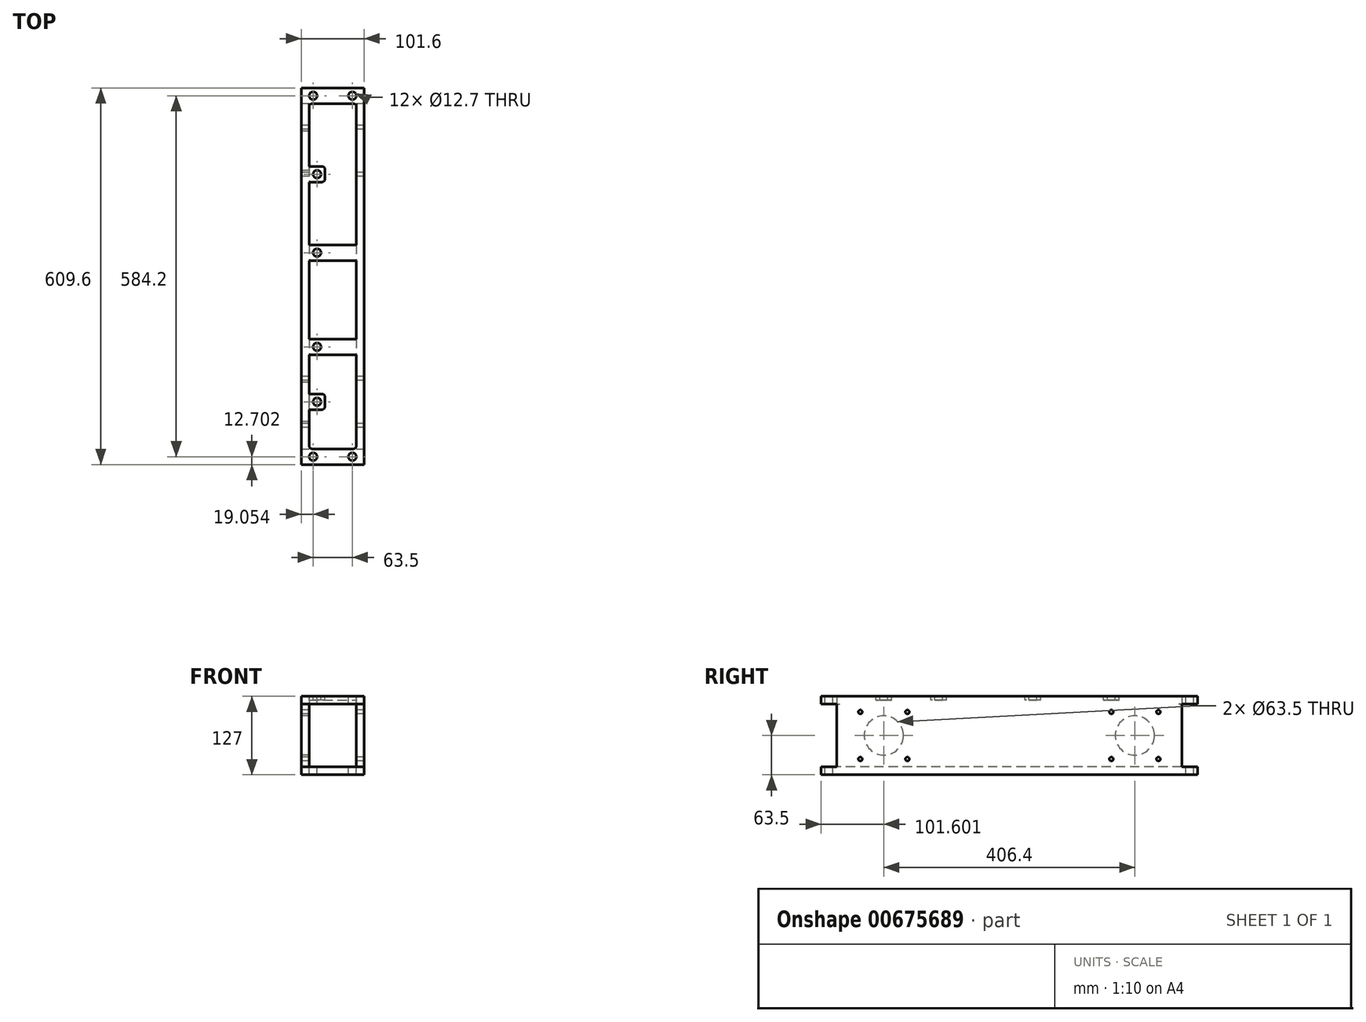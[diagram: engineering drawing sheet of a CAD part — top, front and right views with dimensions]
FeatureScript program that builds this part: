
annotation { "Feature Type Name" : "Feature", "Feature Type Description" : "" }
export const myFeature = defineFeature(function(context is Context, id is Id, definition is map)
    precondition{}
    {
        {
            var Q0;
            Q0=qCreatedBy(makeId("Top.planeOp"),FACE);
            var sketch = newSketch(context, id + "F0", { "sketchPlane" : qUnion([Q0])});
            skLineSegment(sketch, "E0.bottom", {"start": v(-138.95, -277.45) * mm, "end": v(-37.35, -277.45) * mm});
            skLineSegment(sketch, "E0.top", {"start": v(-138.95, 332.15) * mm, "end": v(-37.35, 332.15) * mm});
            skLineSegment(sketch, "E0.left", {"start": v(-138.95, -277.45) * mm, "end": v(-138.95, 332.15) * mm});
            skLineSegment(sketch, "E0.right", {"start": v(-37.35, -277.45) * mm, "end": v(-37.35, 332.15) * mm});
            skLineSegment(sketch, "E1.bottom", {"start": v(-126.25, 306.75) * mm, "end": v(-50.05, 306.75) * mm});
            skLineSegment(sketch, "E1.top", {"start": v(-126.25, -252.05) * mm, "end": v(-50.05, -252.05) * mm});
            skLineSegment(sketch, "E1.left", {"start": v(-126.25, 306.75) * mm, "end": v(-126.25, -252.05) * mm});
            skLineSegment(sketch, "E1.right", {"start": v(-50.05, 306.75) * mm, "end": v(-50.05, -252.05) * mm});
            skSolve(sketch);
        }
        {
            var Q0;
            Q0=makeQuery(id+"F0.imprint","IMPRINT",FACE,{"disambiguationData":[TD([[makeQuery(id+"F0.imprint","IMPRINT",EDGE,{"derivedFrom":sQuery(id+"F0.wireOp",EDGE,"E0.bottom")}),1.0]])]});
            extrude(context, id + "F1", {"entities" : qUnion([Q0]), "depth" : 127 * mm, "offsetDistance" : 25.4 * mm});
        }
        {
            var Q0;
            Q0=makeQuery(id+"F1.opExtrude","CAP_FACE",FACE,{"disambiguationData":[OSD([sQuery(id+"F0.wireOp",EDGE,"E0.bottom"),sQuery(id+"F0.wireOp",EDGE,"E0.top"),sQuery(id+"F0.wireOp",EDGE,"E0.left"),sQuery(id+"F0.wireOp",EDGE,"E0.right"),sQuery(id+"F0.wireOp",EDGE,"E1.bottom"),sQuery(id+"F0.wireOp",EDGE,"E1.top"),sQuery(id+"F0.wireOp",EDGE,"E1.left"),sQuery(id+"F0.wireOp",EDGE,"E1.right")])],"isStart":true});
            var sketch = newSketch(context, id + "F2", { "sketchPlane" : qUnion([Q0])});
            skLineSegment(sketch, "E2.bottom", {"start": v(-126.25, 252.05) * mm, "end": v(-50.05, 252.05) * mm});
            skLineSegment(sketch, "E2.top", {"start": v(-126.25, -306.75) * mm, "end": v(-50.05, -306.75) * mm});
            skLineSegment(sketch, "E2.left", {"start": v(-126.25, 252.05) * mm, "end": v(-126.25, -306.75) * mm});
            skLineSegment(sketch, "E2.right", {"start": v(-50.05, 252.05) * mm, "end": v(-50.05, -306.75) * mm});
            skSolve(sketch);
        }
        {
            var Q0;
            Q0=makeQuery(id+"F2.imprint","IMPRINT",FACE,{"disambiguationData":[TD([[makeQuery(id+"F2.imprint","IMPRINT",EDGE,{"derivedFrom":sQuery(id+"F2.wireOp",EDGE,"E2.bottom")}),-1.0]])]});
            extrude(context, id + "F3", {"entities" : qUnion([Q0]), "operationType" : NewBodyOperationType.ADD, "oppositeDirection" : true, "depth" : 19.05 * mm, "offsetDistance" : 25.4 * mm});
        }
        {
            var Q0;
            Q0=makeQuery(id+"F1.opExtrude","CAP_FACE",FACE,{"disambiguationData":[OSD([sQuery(id+"F0.wireOp",EDGE,"E0.bottom"),sQuery(id+"F0.wireOp",EDGE,"E0.top"),sQuery(id+"F0.wireOp",EDGE,"E0.left"),sQuery(id+"F0.wireOp",EDGE,"E0.right"),sQuery(id+"F0.wireOp",EDGE,"E1.bottom"),sQuery(id+"F0.wireOp",EDGE,"E1.top"),sQuery(id+"F0.wireOp",EDGE,"E1.left"),sQuery(id+"F0.wireOp",EDGE,"E1.right")])],"isStart":false});
            var sketch = newSketch(context, id + "F4", { "sketchPlane" : qUnion([Q0])});
            skLineSegment(sketch, "E3.bottom", {"start": v(-126.25, 78.15) * mm, "end": v(-50.05, 78.15) * mm});
            skLineSegment(sketch, "E3.top", {"start": v(-126.25, 52.75) * mm, "end": v(-50.05, 52.75) * mm});
            skLineSegment(sketch, "E3.left", {"start": v(-126.25, 78.15) * mm, "end": v(-126.25, 52.75) * mm});
            skLineSegment(sketch, "E3.right", {"start": v(-50.05, 78.15) * mm, "end": v(-50.05, 52.75) * mm});
            skLineSegment(sketch, "E4.bottom", {"start": v(-126.25, -74.25) * mm, "end": v(-50.05, -74.25) * mm});
            skLineSegment(sketch, "E4.top", {"start": v(-126.25, -99.65) * mm, "end": v(-50.05, -99.65) * mm});
            skLineSegment(sketch, "E4.left", {"start": v(-126.25, -74.25) * mm, "end": v(-126.25, -99.65) * mm});
            skLineSegment(sketch, "E4.right", {"start": v(-50.05, -74.25) * mm, "end": v(-50.05, -99.65) * mm});
            skSolve(sketch);
        }
        {
            var Q0;
            Q0=makeQuery(id+"F4.imprint","IMPRINT",FACE,{"disambiguationData":[TD([[makeQuery(id+"F4.imprint","IMPRINT",EDGE,{"derivedFrom":sQuery(id+"F4.wireOp",EDGE,"E3.bottom")}),-1.0]])]});
            var Q1;
            Q1=makeQuery(id+"F4.imprint","IMPRINT",FACE,{"disambiguationData":[TD([[makeQuery(id+"F4.imprint","IMPRINT",EDGE,{"derivedFrom":sQuery(id+"F4.wireOp",EDGE,"E4.bottom")}),-1.0]])]});
            extrude(context, id + "F5", {"entities" : qUnion([Q0, Q1]), "operationType" : NewBodyOperationType.ADD, "oppositeDirection" : true, "depth" : 6.35 * mm, "offsetDistance" : 25.4 * mm});
        }
        {
            var Q0;
            Q0=makeQuery(id+"F1.opExtrude","SWEPT_FACE",FACE,{"disambiguationData":[OSD([sQuery(id+"F0.wireOp",EDGE,"E0.bottom")])]});
            var sketch = newSketch(context, id + "F6", { "sketchPlane" : qUnion([Q0])});
            skLineSegment(sketch, "E5.bottom", {"start": v(-138.95, 114.3) * mm, "end": v(-37.35, 114.3) * mm});
            skLineSegment(sketch, "E5.top", {"start": v(-138.95, 12.7) * mm, "end": v(-37.35, 12.7) * mm});
            skLineSegment(sketch, "E5.left", {"start": v(-138.95, 114.3) * mm, "end": v(-138.95, 12.7) * mm});
            skLineSegment(sketch, "E5.right", {"start": v(-37.35, 114.3) * mm, "end": v(-37.35, 12.7) * mm});
            skSolve(sketch);
        }
        {
            var Q0;
            Q0=makeQuery(id+"F6.imprint","IMPRINT",FACE,{"disambiguationData":[TD([[makeQuery(id+"F6.imprint","IMPRINT",EDGE,{"derivedFrom":sQuery(id+"F6.wireOp",EDGE,"E5.bottom")}),-1.0]])]});
            extrude(context, id + "F7", {"entities" : qUnion([Q0]), "operationType" : NewBodyOperationType.REMOVE, "oppositeDirection" : true, "depth" : 25.4 * mm, "offsetDistance" : 25.4 * mm});
        }
        {
            var Q0;
            Q0=makeQuery(id+"F1.opExtrude","SWEPT_FACE",FACE,{"disambiguationData":[OSD([sQuery(id+"F0.wireOp",EDGE,"E0.top")])]});
            var sketch = newSketch(context, id + "F8", { "sketchPlane" : qUnion([Q0])});
            skLineSegment(sketch, "E6.bottom", {"start": v(37.35, 114.3) * mm, "end": v(138.95, 114.3) * mm});
            skLineSegment(sketch, "E6.top", {"start": v(37.35, 12.7) * mm, "end": v(138.95, 12.7) * mm});
            skLineSegment(sketch, "E6.left", {"start": v(37.35, 114.3) * mm, "end": v(37.35, 12.7) * mm});
            skLineSegment(sketch, "E6.right", {"start": v(138.95, 114.3) * mm, "end": v(138.95, 12.7) * mm});
            skSolve(sketch);
        }
        {
            var Q0;
            Q0=makeQuery(id+"F8.imprint","IMPRINT",FACE,{"disambiguationData":[TD([[makeQuery(id+"F8.imprint","IMPRINT",EDGE,{"derivedFrom":sQuery(id+"F8.wireOp",EDGE,"E6.bottom")}),-1.0]])]});
            extrude(context, id + "F9", {"entities" : qUnion([Q0]), "operationType" : NewBodyOperationType.REMOVE, "oppositeDirection" : true, "depth" : 25.4 * mm, "offsetDistance" : 25.4 * mm});
        }
        {
            var Q0;
            Q0=makeQuery(id+"F3.opExtrude","CAP_FACE",FACE,{"disambiguationData":[OSD([sQuery(id+"F2.wireOp",EDGE,"E2.bottom"),sQuery(id+"F2.wireOp",EDGE,"E2.top"),sQuery(id+"F2.wireOp",EDGE,"E2.left"),sQuery(id+"F2.wireOp",EDGE,"E2.right")])],"isStart":false});
            extrude(context, id + "F10", {"entities" : qUnion([Q0]), "operationType" : NewBodyOperationType.REMOVE, "oppositeDirection" : true, "depth" : 6.35 * mm, "offsetDistance" : 25.4 * mm});
        }
        {
            var Q0;
            Q0=makeQuery(id+"F5.boolean.opBoolean","MERGE",FACE,{"derivedFrom":[makeQuery(id+"F1.opExtrude","CAP_FACE",FACE,{"disambiguationData":[OSD([sQuery(id+"F0.wireOp",EDGE,"E0.bottom"),sQuery(id+"F0.wireOp",EDGE,"E0.top"),sQuery(id+"F0.wireOp",EDGE,"E0.left"),sQuery(id+"F0.wireOp",EDGE,"E0.right"),sQuery(id+"F0.wireOp",EDGE,"E1.bottom"),sQuery(id+"F0.wireOp",EDGE,"E1.top"),sQuery(id+"F0.wireOp",EDGE,"E1.left"),sQuery(id+"F0.wireOp",EDGE,"E1.right")])],"isStart":false}),makeQuery(id+"F5.opExtrude","CAP_FACE",FACE,{"disambiguationData":[OSD([sQuery(id+"F4.wireOp",EDGE,"E3.bottom"),sQuery(id+"F4.wireOp",EDGE,"E3.top"),sQuery(id+"F4.wireOp",EDGE,"E3.left"),sQuery(id+"F4.wireOp",EDGE,"E3.right")])],"isStart":true}),makeQuery(id+"F5.opExtrude","CAP_FACE",FACE,{"disambiguationData":[OSD([sQuery(id+"F4.wireOp",EDGE,"E4.bottom"),sQuery(id+"F4.wireOp",EDGE,"E4.top"),sQuery(id+"F4.wireOp",EDGE,"E4.left"),sQuery(id+"F4.wireOp",EDGE,"E4.right")])],"isStart":true})]});
            var sketch = newSketch(context, id + "F11", { "sketchPlane" : qUnion([Q0])});
            skCircle(sketch, "E7", {"center": v(-113.55, 65.45) * mm, "radius": 6.35 * mm});
            skCircle(sketch, "E8", {"center": v(-113.55, -86.95) * mm, "radius": 6.35 * mm});
            skSolve(sketch);
        }
        {
            var Q0;
            Q0=makeQuery(id+"F11.imprint","IMPRINT",FACE,{"disambiguationData":[TD([[makeQuery(id+"F11.imprint","IMPRINT",EDGE,{"derivedFrom":sQuery(id+"F11.wireOp",EDGE,"E7")}),1.0]])]});
            var Q1;
            Q1=makeQuery(id+"F11.imprint","IMPRINT",FACE,{"disambiguationData":[TD([[makeQuery(id+"F11.imprint","IMPRINT",EDGE,{"derivedFrom":sQuery(id+"F11.wireOp",EDGE,"E8")}),1.0]])]});
            extrude(context, id + "F12", {"entities" : qUnion([Q0, Q1]), "operationType" : NewBodyOperationType.REMOVE, "oppositeDirection" : true, "depth" : 6.35 * mm, "offsetDistance" : 25.4 * mm});
        }
        {
            var Q0;
            Q0=makeQuery(id+"F5.boolean.opBoolean","MERGE",FACE,{"derivedFrom":[makeQuery(id+"F1.opExtrude","CAP_FACE",FACE,{"disambiguationData":[OSD([sQuery(id+"F0.wireOp",EDGE,"E0.bottom"),sQuery(id+"F0.wireOp",EDGE,"E0.top"),sQuery(id+"F0.wireOp",EDGE,"E0.left"),sQuery(id+"F0.wireOp",EDGE,"E0.right"),sQuery(id+"F0.wireOp",EDGE,"E1.bottom"),sQuery(id+"F0.wireOp",EDGE,"E1.top"),sQuery(id+"F0.wireOp",EDGE,"E1.left"),sQuery(id+"F0.wireOp",EDGE,"E1.right")])],"isStart":false}),makeQuery(id+"F5.opExtrude","CAP_FACE",FACE,{"disambiguationData":[OSD([sQuery(id+"F4.wireOp",EDGE,"E3.bottom"),sQuery(id+"F4.wireOp",EDGE,"E3.top"),sQuery(id+"F4.wireOp",EDGE,"E3.left"),sQuery(id+"F4.wireOp",EDGE,"E3.right")])],"isStart":true}),makeQuery(id+"F5.opExtrude","CAP_FACE",FACE,{"disambiguationData":[OSD([sQuery(id+"F4.wireOp",EDGE,"E4.bottom"),sQuery(id+"F4.wireOp",EDGE,"E4.top"),sQuery(id+"F4.wireOp",EDGE,"E4.left"),sQuery(id+"F4.wireOp",EDGE,"E4.right")])],"isStart":true})]});
            var sketch = newSketch(context, id + "F13", { "sketchPlane" : qUnion([Q0])});
            skCircle(sketch, "E9", {"center": v(-119.9, 319.45) * mm, "radius": 6.35 * mm});
            skCircle(sketch, "E10", {"center": v(-56.4, 319.45) * mm, "radius": 6.35 * mm});
            skCircle(sketch, "E11", {"center": v(-119.9, -264.75) * mm, "radius": 6.35 * mm});
            skCircle(sketch, "E12", {"center": v(-56.4, -264.75) * mm, "radius": 6.35 * mm});
            skSolve(sketch);
        }
        {
            var Q0;
            Q0=makeQuery(id+"F13.imprint","IMPRINT",FACE,{"disambiguationData":[TD([[makeQuery(id+"F13.imprint","IMPRINT",EDGE,{"derivedFrom":sQuery(id+"F13.wireOp",EDGE,"E11")}),1.0]])]});
            var Q1;
            Q1=makeQuery(id+"F13.imprint","IMPRINT",FACE,{"disambiguationData":[TD([[makeQuery(id+"F13.imprint","IMPRINT",EDGE,{"derivedFrom":sQuery(id+"F13.wireOp",EDGE,"E12")}),1.0]])]});
            var Q2;
            Q2=makeQuery(id+"F13.imprint","IMPRINT",FACE,{"disambiguationData":[TD([[makeQuery(id+"F13.imprint","IMPRINT",EDGE,{"derivedFrom":sQuery(id+"F13.wireOp",EDGE,"E9")}),1.0]])]});
            var Q3;
            Q3=makeQuery(id+"F13.imprint","IMPRINT",FACE,{"disambiguationData":[TD([[makeQuery(id+"F13.imprint","IMPRINT",EDGE,{"derivedFrom":sQuery(id+"F13.wireOp",EDGE,"E10")}),1.0]])]});
            extrude(context, id + "F14", {"entities" : qUnion([Q0, Q1, Q2, Q3]), "operationType" : NewBodyOperationType.REMOVE, "oppositeDirection" : true, "depth" : 12.7 * mm, "offsetDistance" : 25.4 * mm});
        }
        {
            var Q0;
            Q0=makeQuery(id+"F13.imprint","IMPRINT",FACE,{"disambiguationData":[TD([[makeQuery(id+"F13.imprint","IMPRINT",EDGE,{"derivedFrom":sQuery(id+"F13.wireOp",EDGE,"E9")}),1.0]])]});
            var Q1;
            Q1=makeQuery(id+"F13.imprint","IMPRINT",FACE,{"disambiguationData":[TD([[makeQuery(id+"F13.imprint","IMPRINT",EDGE,{"derivedFrom":sQuery(id+"F13.wireOp",EDGE,"E10")}),1.0]])]});
            var Q2;
            Q2=makeQuery(id+"F13.imprint","IMPRINT",FACE,{"disambiguationData":[TD([[makeQuery(id+"F13.imprint","IMPRINT",EDGE,{"derivedFrom":sQuery(id+"F13.wireOp",EDGE,"E11")}),1.0]])]});
            var Q3;
            Q3=makeQuery(id+"F13.imprint","IMPRINT",FACE,{"disambiguationData":[TD([[makeQuery(id+"F13.imprint","IMPRINT",EDGE,{"derivedFrom":sQuery(id+"F13.wireOp",EDGE,"E12")}),1.0]])]});
            extrude(context, id + "F15", {"entities" : qUnion([Q0, Q1, Q2, Q3]), "operationType" : NewBodyOperationType.REMOVE, "oppositeDirection" : true, "depth" : 127 * mm, "offsetDistance" : 25.4 * mm});
        }
        {
            var Q0;
            Q0=makeQuery(id+"F5.boolean.opBoolean","MERGE",FACE,{"derivedFrom":[makeQuery(id+"F1.opExtrude","CAP_FACE",FACE,{"disambiguationData":[OSD([sQuery(id+"F0.wireOp",EDGE,"E0.bottom"),sQuery(id+"F0.wireOp",EDGE,"E0.top"),sQuery(id+"F0.wireOp",EDGE,"E0.left"),sQuery(id+"F0.wireOp",EDGE,"E0.right"),sQuery(id+"F0.wireOp",EDGE,"E1.bottom"),sQuery(id+"F0.wireOp",EDGE,"E1.top"),sQuery(id+"F0.wireOp",EDGE,"E1.left"),sQuery(id+"F0.wireOp",EDGE,"E1.right")])],"isStart":false}),makeQuery(id+"F5.opExtrude","CAP_FACE",FACE,{"disambiguationData":[OSD([sQuery(id+"F4.wireOp",EDGE,"E3.bottom"),sQuery(id+"F4.wireOp",EDGE,"E3.top"),sQuery(id+"F4.wireOp",EDGE,"E3.left"),sQuery(id+"F4.wireOp",EDGE,"E3.right")])],"isStart":true}),makeQuery(id+"F5.opExtrude","CAP_FACE",FACE,{"disambiguationData":[OSD([sQuery(id+"F4.wireOp",EDGE,"E4.bottom"),sQuery(id+"F4.wireOp",EDGE,"E4.top"),sQuery(id+"F4.wireOp",EDGE,"E4.left"),sQuery(id+"F4.wireOp",EDGE,"E4.right")])],"isStart":true})]});
            var sketch = newSketch(context, id + "F16", { "sketchPlane" : qUnion([Q0])});
            skLineSegment(sketch, "E13.bottom", {"start": v(-126.25, 205.15) * mm, "end": v(-100.85, 205.15) * mm});
            skLineSegment(sketch, "E13.top", {"start": v(-126.25, 179.75) * mm, "end": v(-100.85, 179.75) * mm});
            skLineSegment(sketch, "E13.left", {"start": v(-126.25, 205.15) * mm, "end": v(-126.25, 179.75) * mm});
            skLineSegment(sketch, "E13.right", {"start": v(-100.85, 205.15) * mm, "end": v(-100.85, 179.75) * mm});
            skLineSegment(sketch, "E14.bottom", {"start": v(-126.25, -163.15) * mm, "end": v(-100.85, -163.15) * mm});
            skLineSegment(sketch, "E14.top", {"start": v(-126.25, -188.55) * mm, "end": v(-100.85, -188.55) * mm});
            skLineSegment(sketch, "E14.left", {"start": v(-126.25, -163.15) * mm, "end": v(-126.25, -188.55) * mm});
            skLineSegment(sketch, "E14.right", {"start": v(-100.85, -163.15) * mm, "end": v(-100.85, -188.55) * mm});
            skSolve(sketch);
        }
        {
            var Q0;
            Q0=makeQuery(id+"F16.imprint","IMPRINT",FACE,{"disambiguationData":[TD([[makeQuery(id+"F16.imprint","IMPRINT",EDGE,{"derivedFrom":sQuery(id+"F16.wireOp",EDGE,"E14.bottom")}),-1.0]])]});
            var Q1;
            Q1=makeQuery(id+"F16.imprint","IMPRINT",FACE,{"disambiguationData":[TD([[makeQuery(id+"F16.imprint","IMPRINT",EDGE,{"derivedFrom":sQuery(id+"F16.wireOp",EDGE,"E13.bottom")}),-1.0]])]});
            extrude(context, id + "F17", {"entities" : qUnion([Q0, Q1]), "operationType" : NewBodyOperationType.ADD, "oppositeDirection" : true, "depth" : 6.35 * mm, "offsetDistance" : 25.4 * mm});
        }
        {
            var Q0;
            Q0=makeQuery(id+"F17.boolean.opBoolean","MERGE",FACE,{"derivedFrom":[makeQuery(id+"F5.boolean.opBoolean","MERGE",FACE,{"derivedFrom":[makeQuery(id+"F1.opExtrude","CAP_FACE",FACE,{"disambiguationData":[OSD([sQuery(id+"F0.wireOp",EDGE,"E0.bottom"),sQuery(id+"F0.wireOp",EDGE,"E0.top"),sQuery(id+"F0.wireOp",EDGE,"E0.left"),sQuery(id+"F0.wireOp",EDGE,"E0.right"),sQuery(id+"F0.wireOp",EDGE,"E1.bottom"),sQuery(id+"F0.wireOp",EDGE,"E1.top"),sQuery(id+"F0.wireOp",EDGE,"E1.left"),sQuery(id+"F0.wireOp",EDGE,"E1.right")])],"isStart":false}),makeQuery(id+"F5.opExtrude","CAP_FACE",FACE,{"disambiguationData":[OSD([sQuery(id+"F4.wireOp",EDGE,"E3.bottom"),sQuery(id+"F4.wireOp",EDGE,"E3.top"),sQuery(id+"F4.wireOp",EDGE,"E3.left"),sQuery(id+"F4.wireOp",EDGE,"E3.right")])],"isStart":true}),makeQuery(id+"F5.opExtrude","CAP_FACE",FACE,{"disambiguationData":[OSD([sQuery(id+"F4.wireOp",EDGE,"E4.bottom"),sQuery(id+"F4.wireOp",EDGE,"E4.top"),sQuery(id+"F4.wireOp",EDGE,"E4.left"),sQuery(id+"F4.wireOp",EDGE,"E4.right")])],"isStart":true})]}),makeQuery(id+"F17.opExtrude","CAP_FACE",FACE,{"disambiguationData":[OSD([sQuery(id+"F16.wireOp",EDGE,"E13.bottom"),sQuery(id+"F16.wireOp",EDGE,"E13.top"),sQuery(id+"F16.wireOp",EDGE,"E13.left"),sQuery(id+"F16.wireOp",EDGE,"E13.right")])],"isStart":true}),makeQuery(id+"F17.opExtrude","CAP_FACE",FACE,{"disambiguationData":[OSD([sQuery(id+"F16.wireOp",EDGE,"E14.bottom"),sQuery(id+"F16.wireOp",EDGE,"E14.top"),sQuery(id+"F16.wireOp",EDGE,"E14.left"),sQuery(id+"F16.wireOp",EDGE,"E14.right")])],"isStart":true})]});
            var sketch = newSketch(context, id + "F18", { "sketchPlane" : qUnion([Q0])});
            skCircle(sketch, "E15", {"center": v(-113.55, -175.85) * mm, "radius": 6.35 * mm});
            skPoint(sketch, "E15.centerSnap0", {"position": v(-113.55, -163.15) * mm});
            skPoint(sketch, "E15.centerSnap1", {"position": v(-100.85, -175.85) * mm});
            skCircle(sketch, "E16", {"center": v(-113.55, 192.45) * mm, "radius": 6.35 * mm});
            skPoint(sketch, "E16.centerSnap0", {"position": v(-100.85, 192.45) * mm});
            skSolve(sketch);
        }
        {
            var Q0;
            Q0=makeQuery(id+"F18.imprint","IMPRINT",FACE,{"disambiguationData":[TD([[makeQuery(id+"F18.imprint","IMPRINT",EDGE,{"derivedFrom":sQuery(id+"F18.wireOp",EDGE,"E16")}),1.0]])]});
            var Q1;
            Q1=makeQuery(id+"F18.imprint","IMPRINT",FACE,{"disambiguationData":[TD([[makeQuery(id+"F18.imprint","IMPRINT",EDGE,{"derivedFrom":sQuery(id+"F18.wireOp",EDGE,"E15")}),1.0]])]});
            extrude(context, id + "F19", {"entities" : qUnion([Q0, Q1]), "operationType" : NewBodyOperationType.REMOVE, "oppositeDirection" : true, "depth" : 6.35 * mm, "offsetDistance" : 25.4 * mm});
        }
        {
            var Q0;
            Q0=makeQuery(id+"F5.opExtrude","SWEPT_EDGE",EDGE,{"disambiguationData":[OSD([sQuery(id+"F0.wireOp",EDGE,"E1.left"),sQuery(id+"F4.wireOp",EDGE,"E4.top"),sQuery(id+"F4.wireOp",EDGE,"E4.left")])]});
            var Q1;
            Q1=makeQuery(id+"F5.opExtrude","SWEPT_EDGE",EDGE,{"disambiguationData":[OSD([sQuery(id+"F0.wireOp",EDGE,"E1.right"),sQuery(id+"F4.wireOp",EDGE,"E4.top"),sQuery(id+"F4.wireOp",EDGE,"E4.right")])]});
            var Q2;
            Q2=makeQuery(id+"F17.opExtrude","SWEPT_EDGE",EDGE,{"disambiguationData":[OSD([sQuery(id+"F16.wireOp",EDGE,"E14.bottom"),sQuery(id+"F16.wireOp",EDGE,"E14.right")])]});
            var Q3;
            Q3=makeQuery(id+"F17.opExtrude","SWEPT_EDGE",EDGE,{"disambiguationData":[OSD([sQuery(id+"F16.wireOp",EDGE,"E14.top"),sQuery(id+"F16.wireOp",EDGE,"E14.right")])]});
            var Q4;
            Q4=makeQuery(id+"F17.opExtrude","SWEPT_EDGE",EDGE,{"disambiguationData":[OSD([sQuery(id+"F0.wireOp",EDGE,"E1.left"),sQuery(id+"F16.wireOp",EDGE,"E14.top"),sQuery(id+"F16.wireOp",EDGE,"E14.left")])]});
            var Q5;
            Q5=makeQuery(id+"F17.opExtrude","SWEPT_EDGE",EDGE,{"disambiguationData":[OSD([sQuery(id+"F0.wireOp",EDGE,"E1.left"),sQuery(id+"F16.wireOp",EDGE,"E14.bottom"),sQuery(id+"F16.wireOp",EDGE,"E14.left")])]});
            var Q6;
            {var subQ0=sQuery(id+"F0.wireOp",EDGE,"E1.top");var subQ1=sQuery(id+"F0.wireOp",EDGE,"E1.left");Q6=makeQuery(id+"F7.boolean.opBoolean","SPLIT",EDGE,{"disambiguationData":[topologyDisambiguationEdgeConnected([makeQuery(id+"F1.opExtrude","SWEPT_FACE",FACE,{"disambiguationData":[OSD([subQ0])]})])],"derivedFrom":makeQuery(id+"F1.opExtrude","SWEPT_EDGE",EDGE,{"disambiguationData":[OSD([subQ0,subQ1])]})});}
            var Q7;
            {var subQ0=sQuery(id+"F0.wireOp",EDGE,"E1.top");var subQ1=sQuery(id+"F0.wireOp",EDGE,"E1.right");Q7=makeQuery(id+"F7.boolean.opBoolean","SPLIT",EDGE,{"disambiguationData":[topologyDisambiguationEdgeConnected([makeQuery(id+"F1.opExtrude","SWEPT_FACE",FACE,{"disambiguationData":[OSD([subQ0])]})])],"derivedFrom":makeQuery(id+"F1.opExtrude","SWEPT_EDGE",EDGE,{"disambiguationData":[OSD([subQ0,subQ1])]})});}
            var Q8;
            Q8=makeQuery(id+"F5.opExtrude","SWEPT_EDGE",EDGE,{"disambiguationData":[OSD([sQuery(id+"F0.wireOp",EDGE,"E1.right"),sQuery(id+"F4.wireOp",EDGE,"E4.bottom"),sQuery(id+"F4.wireOp",EDGE,"E4.right")])]});
            var Q9;
            Q9=makeQuery(id+"F5.opExtrude","SWEPT_EDGE",EDGE,{"disambiguationData":[OSD([sQuery(id+"F0.wireOp",EDGE,"E1.left"),sQuery(id+"F4.wireOp",EDGE,"E4.bottom"),sQuery(id+"F4.wireOp",EDGE,"E4.left")])]});
            var Q10;
            Q10=makeQuery(id+"F5.opExtrude","SWEPT_EDGE",EDGE,{"disambiguationData":[OSD([sQuery(id+"F0.wireOp",EDGE,"E1.right"),sQuery(id+"F4.wireOp",EDGE,"E3.top"),sQuery(id+"F4.wireOp",EDGE,"E3.right")])]});
            var Q11;
            Q11=makeQuery(id+"F5.opExtrude","SWEPT_EDGE",EDGE,{"disambiguationData":[OSD([sQuery(id+"F0.wireOp",EDGE,"E1.left"),sQuery(id+"F4.wireOp",EDGE,"E3.top"),sQuery(id+"F4.wireOp",EDGE,"E3.left")])]});
            var Q12;
            Q12=makeQuery(id+"F17.opExtrude","SWEPT_EDGE",EDGE,{"disambiguationData":[OSD([sQuery(id+"F0.wireOp",EDGE,"E1.left"),sQuery(id+"F16.wireOp",EDGE,"E13.top"),sQuery(id+"F16.wireOp",EDGE,"E13.left")])]});
            var Q13;
            Q13=makeQuery(id+"F5.opExtrude","SWEPT_EDGE",EDGE,{"disambiguationData":[OSD([sQuery(id+"F0.wireOp",EDGE,"E1.left"),sQuery(id+"F4.wireOp",EDGE,"E3.bottom"),sQuery(id+"F4.wireOp",EDGE,"E3.left")])]});
            var Q14;
            Q14=makeQuery(id+"F5.opExtrude","SWEPT_EDGE",EDGE,{"disambiguationData":[OSD([sQuery(id+"F0.wireOp",EDGE,"E1.right"),sQuery(id+"F4.wireOp",EDGE,"E3.bottom"),sQuery(id+"F4.wireOp",EDGE,"E3.right")])]});
            var Q15;
            Q15=makeQuery(id+"F17.opExtrude","SWEPT_EDGE",EDGE,{"disambiguationData":[OSD([sQuery(id+"F16.wireOp",EDGE,"E13.top"),sQuery(id+"F16.wireOp",EDGE,"E13.right")])]});
            var Q16;
            Q16=makeQuery(id+"F17.opExtrude","SWEPT_EDGE",EDGE,{"disambiguationData":[OSD([sQuery(id+"F0.wireOp",EDGE,"E1.left"),sQuery(id+"F16.wireOp",EDGE,"E13.bottom"),sQuery(id+"F16.wireOp",EDGE,"E13.left")])]});
            var Q17;
            Q17=makeQuery(id+"F17.opExtrude","SWEPT_EDGE",EDGE,{"disambiguationData":[OSD([sQuery(id+"F16.wireOp",EDGE,"E13.bottom"),sQuery(id+"F16.wireOp",EDGE,"E13.right")])]});
            var Q18;
            {var subQ0=sQuery(id+"F0.wireOp",EDGE,"E1.bottom");var subQ1=sQuery(id+"F0.wireOp",EDGE,"E1.right");Q18=makeQuery(id+"F9.boolean.opBoolean","SPLIT",EDGE,{"disambiguationData":[topologyDisambiguationEdgeConnected([makeQuery(id+"F1.opExtrude","SWEPT_FACE",FACE,{"disambiguationData":[OSD([subQ0])]})])],"derivedFrom":makeQuery(id+"F1.opExtrude","SWEPT_EDGE",EDGE,{"disambiguationData":[OSD([subQ0,subQ1])]})});}
            var Q19;
            {var subQ0=sQuery(id+"F0.wireOp",EDGE,"E1.bottom");var subQ1=sQuery(id+"F0.wireOp",EDGE,"E1.left");Q19=makeQuery(id+"F9.boolean.opBoolean","SPLIT",EDGE,{"disambiguationData":[topologyDisambiguationEdgeConnected([makeQuery(id+"F1.opExtrude","SWEPT_FACE",FACE,{"disambiguationData":[OSD([subQ0])]})])],"derivedFrom":makeQuery(id+"F1.opExtrude","SWEPT_EDGE",EDGE,{"disambiguationData":[OSD([subQ0,subQ1])]})});}
            fillet(context, id + "F20", {"entities" : qUnion([Q0, Q1, Q2, Q3, Q4, Q5, Q6, Q7, Q8, Q9, Q10, Q11, Q12, Q13, Q14, Q15, Q16, Q17, Q18, Q19]), "radius" : 5.08 * mm, "tangentPropagation" : true, "allowEdgeOverflow" : false});
        }
        {
            var Q0;
            Q0=makeQuery(id+"F1.opExtrude","SWEPT_FACE",FACE,{"disambiguationData":[OSD([sQuery(id+"F0.wireOp",EDGE,"E0.left")])]});
            var sketch = newSketch(context, id + "F21", { "sketchPlane" : qUnion([Q0])});
            skCircle(sketch, "E17", {"center": v(175.85, 63.5) * mm, "radius": 31.75 * mm});
            skCircle(sketch, "E18", {"center": v(-230.55, 63.5) * mm, "radius": 31.75 * mm});
            skSolve(sketch);
        }
        {
            var Q0;
            Q0=makeQuery(id+"F21.imprint","IMPRINT",FACE,{"disambiguationData":[TD([[makeQuery(id+"F21.imprint","IMPRINT",EDGE,{"derivedFrom":sQuery(id+"F21.wireOp",EDGE,"E18")}),1.0]])]});
            var Q1;
            Q1=makeQuery(id+"F21.imprint","IMPRINT",FACE,{"disambiguationData":[TD([[makeQuery(id+"F21.imprint","IMPRINT",EDGE,{"derivedFrom":sQuery(id+"F21.wireOp",EDGE,"E17")}),1.0]])]});
            extrude(context, id + "F22", {"entities" : qUnion([Q0, Q1]), "operationType" : NewBodyOperationType.REMOVE, "oppositeDirection" : true, "depth" : 12.7 * mm, "offsetDistance" : 25.4 * mm});
        }
        {
            var Q0;
            Q0=makeQuery(id+"F1.opExtrude","SWEPT_FACE",FACE,{"disambiguationData":[OSD([sQuery(id+"F0.wireOp",EDGE,"E0.left")])]});
            var sketch = newSketch(context, id + "F23", { "sketchPlane" : qUnion([Q0])});
            skCircle(sketch, "E19", {"center": v(-268.65, 101.6) * mm, "radius": 3.18 * mm});
            skCircle(sketch, "E20", {"center": v(-192.45, 101.6) * mm, "radius": 3.18 * mm});
            skCircle(sketch, "E21", {"center": v(-192.45, 25.4) * mm, "radius": 3.18 * mm});
            skCircle(sketch, "E22", {"center": v(-268.65, 25.4) * mm, "radius": 3.18 * mm});
            skCircle(sketch, "E23", {"center": v(137.75, 101.6) * mm, "radius": 3.18 * mm});
            skCircle(sketch, "E24", {"center": v(213.95, 101.6) * mm, "radius": 3.17 * mm});
            skCircle(sketch, "E25", {"center": v(213.95, 25.4) * mm, "radius": 3.18 * mm});
            skCircle(sketch, "E26", {"center": v(137.75, 25.4) * mm, "radius": 3.18 * mm});
            skSolve(sketch);
        }
        {
            var Q0;
            Q0=makeQuery(id+"F23.imprint","IMPRINT",FACE,{"disambiguationData":[TD([[makeQuery(id+"F23.imprint","IMPRINT",EDGE,{"derivedFrom":sQuery(id+"F23.wireOp",EDGE,"E23")}),1.0]])]});
            var Q1;
            Q1=makeQuery(id+"F23.imprint","IMPRINT",FACE,{"disambiguationData":[TD([[makeQuery(id+"F23.imprint","IMPRINT",EDGE,{"derivedFrom":sQuery(id+"F23.wireOp",EDGE,"E26")}),1.0]])]});
            var Q2;
            Q2=makeQuery(id+"F23.imprint","IMPRINT",FACE,{"disambiguationData":[TD([[makeQuery(id+"F23.imprint","IMPRINT",EDGE,{"derivedFrom":sQuery(id+"F23.wireOp",EDGE,"E25")}),1.0]])]});
            var Q3;
            Q3=makeQuery(id+"F23.imprint","IMPRINT",FACE,{"disambiguationData":[TD([[makeQuery(id+"F23.imprint","IMPRINT",EDGE,{"derivedFrom":sQuery(id+"F23.wireOp",EDGE,"E24")}),1.0]])]});
            var Q4;
            Q4=makeQuery(id+"F23.imprint","IMPRINT",FACE,{"disambiguationData":[TD([[makeQuery(id+"F23.imprint","IMPRINT",EDGE,{"derivedFrom":sQuery(id+"F23.wireOp",EDGE,"E21")}),1.0]])]});
            var Q5;
            Q5=makeQuery(id+"F23.imprint","IMPRINT",FACE,{"disambiguationData":[TD([[makeQuery(id+"F23.imprint","IMPRINT",EDGE,{"derivedFrom":sQuery(id+"F23.wireOp",EDGE,"E22")}),1.0]])]});
            var Q6;
            Q6=makeQuery(id+"F23.imprint","IMPRINT",FACE,{"disambiguationData":[TD([[makeQuery(id+"F23.imprint","IMPRINT",EDGE,{"derivedFrom":sQuery(id+"F23.wireOp",EDGE,"E19")}),1.0]])]});
            var Q7;
            Q7=makeQuery(id+"F23.imprint","IMPRINT",FACE,{"disambiguationData":[TD([[makeQuery(id+"F23.imprint","IMPRINT",EDGE,{"derivedFrom":sQuery(id+"F23.wireOp",EDGE,"E20")}),1.0]])]});
            extrude(context, id + "F24", {"entities" : qUnion([Q0, Q1, Q2, Q3, Q4, Q5, Q6, Q7]), "operationType" : NewBodyOperationType.REMOVE, "oppositeDirection" : true, "depth" : 101.6 * mm, "offsetDistance" : 25.4 * mm});
        }
    });
